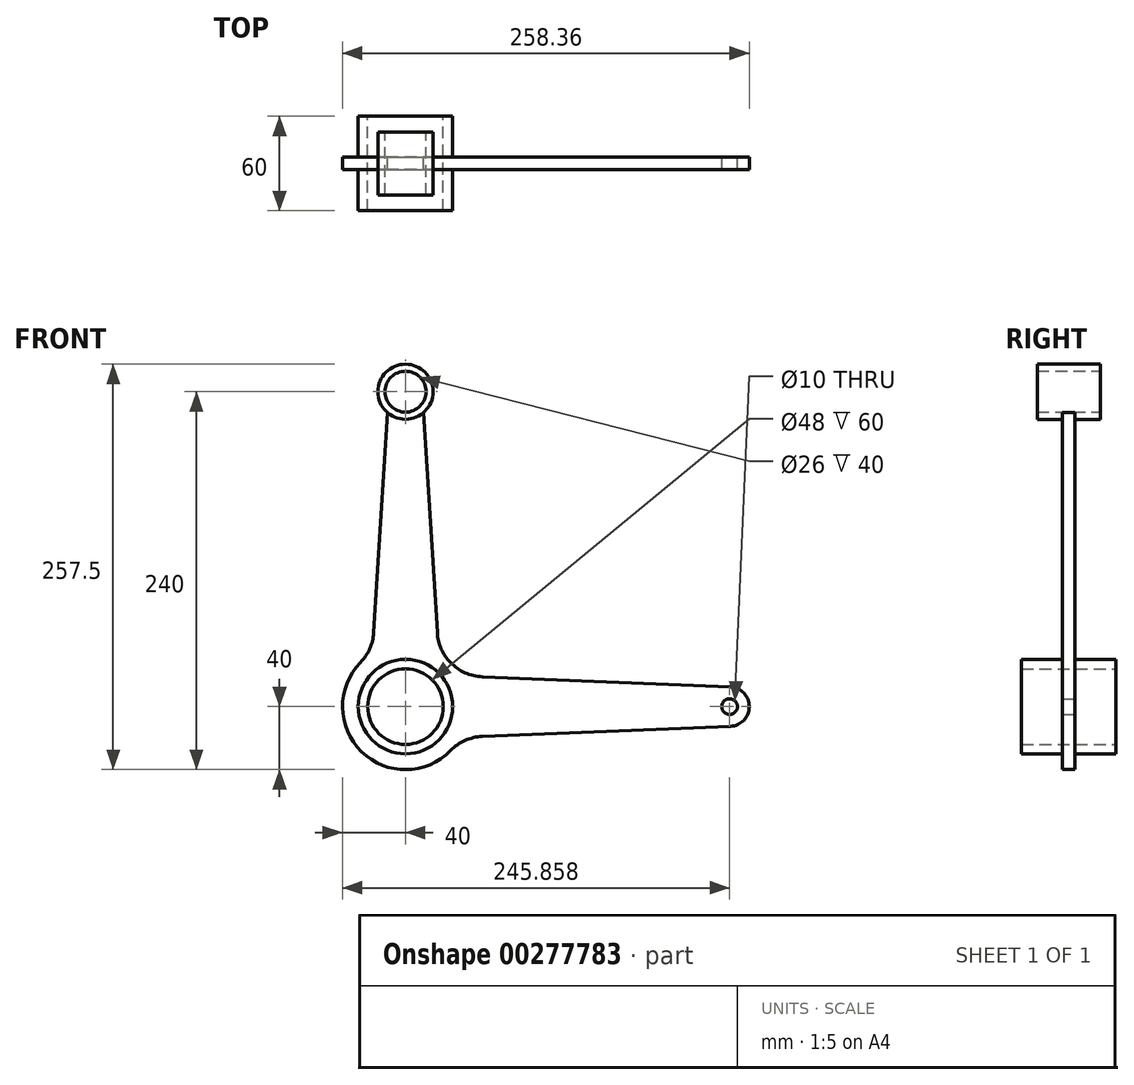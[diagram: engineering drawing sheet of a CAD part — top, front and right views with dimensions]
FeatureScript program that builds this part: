
annotation { "Feature Type Name" : "Feature", "Feature Type Description" : "" }
export const myFeature = defineFeature(function(context is Context, id is Id, definition is map)
    precondition{}
    {
        {
            var Q0;
            Q0=qCreatedBy(makeId("Front.planeOp"),FACE);
            var sketch = newSketch(context, id + "F0", { "sketchPlane" : qUnion([Q0])});
            skCircle(sketch, "E0", {"center": v(0, 0) * mm, "radius": 40 * mm});
            skCircle(sketch, "E1", {"center": v(0, 200) * mm, "radius": 17.5 * mm});
            skCircle(sketch, "E2", {"center": v(205.86, 0) * mm, "radius": 12.5 * mm});
            skCircle(sketch, "E3", {"center": v(0, 200) * mm, "radius": 13 * mm});
            skCircle(sketch, "E4", {"center": v(0, 0) * mm, "radius": 30 * mm});
            skCircle(sketch, "E5", {"center": v(205.86, 0) * mm, "radius": 5 * mm});
            skLineSegment(sketch, "E6", {"start": v(-11.5, 186.8) * mm, "end": v(-21, 34.04) * mm});
            skLineSegment(sketch, "E7.MirrorCS", {"start": v(11.5, 186.8) * mm, "end": v(21, 34.04) * mm});
            skLineSegment(sketch, "E8", {"start": v(34.92, 19.5) * mm, "end": v(206.37, 12.49) * mm});
            skLineSegment(sketch, "E9.MirrorCS", {"start": v(34.92, -19.5) * mm, "end": v(206.37, -12.49) * mm});
            skSolve(sketch);
        }
        {
            var Q0;
            Q0=makeQuery(id+"F0.imprint","IMPRINT",FACE,{"disambiguationData":[TD([[makeQuery(id+"F0.imprint","IMPRINT",EDGE,{"derivedFrom":sQuery(id+"F0.wireOp",EDGE,"E4")}),-1.0]])]});
            var Q1;
            {var subQ0=sQuery(id+"F0.wireOp",EDGE,"E8");Q1=makeQuery(id+"F0.imprint","IMPRINT",FACE,{"disambiguationData":[TD([[makeQuery(id+"F0.imprint","IMPRINT",EDGE,{"derivedFrom":subQ0}),-1.0]])]});}
            var Q2;
            Q2=makeQuery(id+"F0.imprint","IMPRINT",FACE,{"disambiguationData":[TD([[makeQuery(id+"F0.imprint","IMPRINT",EDGE,{"derivedFrom":sQuery(id+"F0.wireOp",EDGE,"E5")}),-1.0]])]});
            var Q3;
            {var subQ0=sQuery(id+"F0.wireOp",EDGE,"E6");Q3=makeQuery(id+"F0.imprint","IMPRINT",FACE,{"disambiguationData":[TD([[makeQuery(id+"F0.imprint","IMPRINT",EDGE,{"derivedFrom":subQ0}),1.0]])]});}
            extrude(context, id + "F1", {"entities" : qUnion([Q0, Q1, Q2, Q3]), "endBound" : BoundingType.SYMMETRIC, "depth" : 8 * mm});
        }
        {
            var Q0;
            Q0=makeQuery(id+"F1.opExtrude","SWEPT_EDGE",EDGE,{"disambiguationData":[OSD([sQuery(id+"F0.wireOp",EDGE,"E0"),sQuery(id+"F0.wireOp",EDGE,"E6")])]});
            var Q1;
            Q1=makeQuery(id+"F1.opExtrude","SWEPT_EDGE",EDGE,{"disambiguationData":[OSD([sQuery(id+"F0.wireOp",EDGE,"E0"),sQuery(id+"F0.wireOp",EDGE,"E9.MirrorCS")])]});
            fillet(context, id + "F2", {"entities" : qUnion([Q0, Q1]), "radius" : 30 * mm, "tangentPropagation" : true, "allowEdgeOverflow" : false});
        }
        {
            var Q0;
            Q0=makeQuery(id+"F1.opExtrude","SWEPT_EDGE",EDGE,{"disambiguationData":[OSD([sQuery(id+"F0.wireOp",EDGE,"E0"),sQuery(id+"F0.wireOp",EDGE,"E8")])]});
            fillet(context, id + "F3", {"entities" : qUnion([Q0]), "radius" : 30 * mm, "tangentPropagation" : true, "allowEdgeOverflow" : false});
        }
        {
            var Q0;
            Q0=makeQuery(id+"F1.opExtrude","SWEPT_EDGE",EDGE,{"disambiguationData":[OSD([sQuery(id+"F0.wireOp",EDGE,"E0"),sQuery(id+"F0.wireOp",EDGE,"E7.MirrorCS")])]});
            fillet(context, id + "F4", {"entities" : qUnion([Q0]), "radius" : 30 * mm, "tangentPropagation" : true, "allowEdgeOverflow" : false});
        }
        {
            var Q0;
            Q0=qCreatedBy(makeId("Front.planeOp"),FACE);
            var sketch = newSketch(context, id + "F5", { "sketchPlane" : qUnion([Q0])});
            skCircle(sketch, "E10", {"center": v(0, 0) * mm, "radius": 24 * mm});
            skCircle(sketch, "E11", {"center": v(0, 0) * mm, "radius": 30 * mm});
            skSolve(sketch);
        }
        {
            var Q0;
            Q0=makeQuery(id+"F5.imprint","IMPRINT",FACE,{"disambiguationData":[TD([[makeQuery(id+"F5.imprint","IMPRINT",EDGE,{"derivedFrom":sQuery(id+"F5.wireOp",EDGE,"E10")}),-1.0]])]});
            extrude(context, id + "F6", {"entities" : qUnion([Q0]), "operationType" : NewBodyOperationType.ADD, "endBound" : BoundingType.SYMMETRIC, "depth" : 60 * mm});
        }
        {
            var Q0;
            Q0=makeQuery(id+"F0.imprint","IMPRINT",FACE,{"disambiguationData":[TD([[makeQuery(id+"F0.imprint","IMPRINT",EDGE,{"derivedFrom":sQuery(id+"F0.wireOp",EDGE,"E3")}),-1.0]])]});
            extrude(context, id + "F7", {"entities" : qUnion([Q0]), "operationType" : NewBodyOperationType.ADD, "endBound" : BoundingType.SYMMETRIC, "depth" : 40 * mm});
        }
    });
